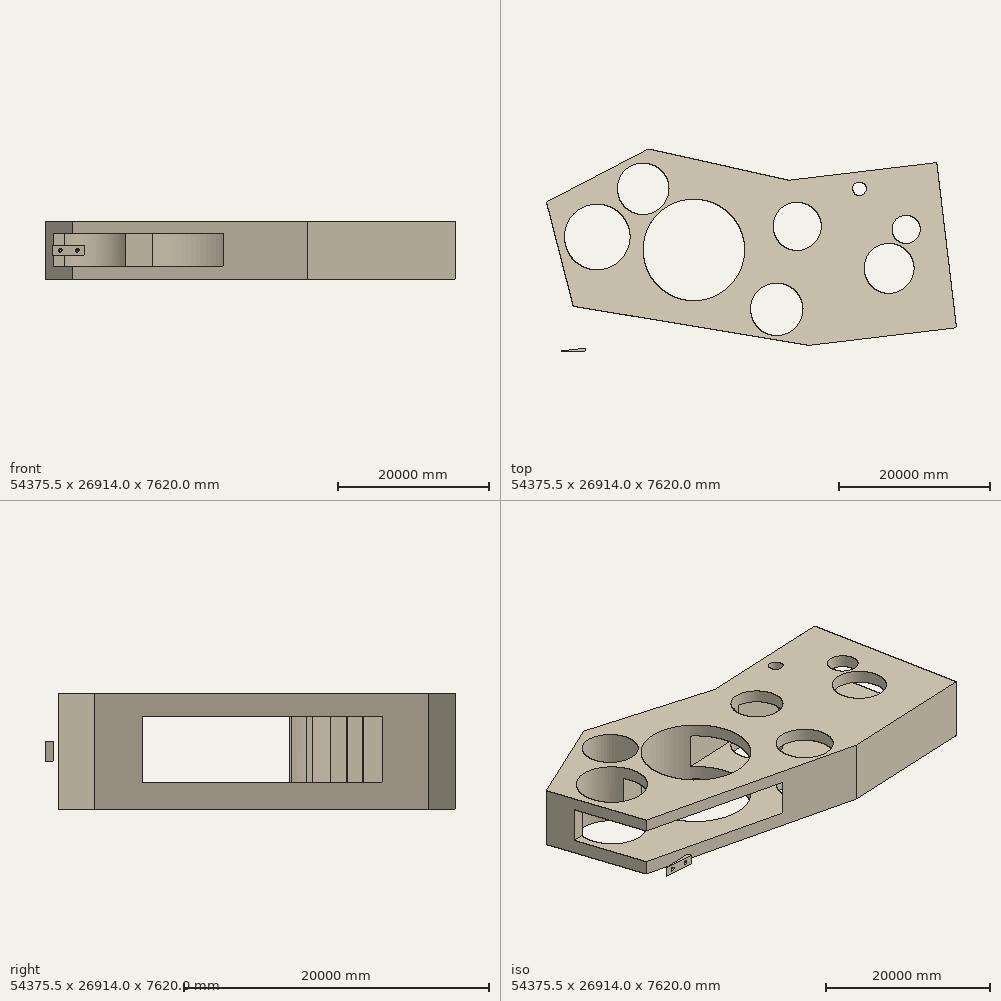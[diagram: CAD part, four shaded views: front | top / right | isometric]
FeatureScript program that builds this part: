
annotation { "Feature Type Name" : "Feature", "Feature Type Description" : "" }
export const myFeature = defineFeature(function(context is Context, id is Id, definition is map)
    precondition{}
    {
        {
            var Q0;
            Q0=qCreatedBy(makeId("Right.planeOp"),FACE);
            var sketch = newSketch(context, id + "F0", { "sketchPlane" : qUnion([Q0])});
            skCircle(sketch, "E0.cCircle", {"center": v(0, 0) * mm, "radius": 129.38 * mm, "construction": true});
            skLineSegment(sketch, "E0.0", {"start": v(-113.82, -61.52) * mm, "end": v(-128.36, -16.25) * mm});
            skLineSegment(sketch, "E0.1", {"start": v(-128.36, -16.25) * mm, "end": v(-125.56, 31.22) * mm});
            skLineSegment(sketch, "E0.2", {"start": v(-125.56, 31.22) * mm, "end": v(-105.8, 74.47) * mm});
            skLineSegment(sketch, "E0.3", {"start": v(-105.8, 74.47) * mm, "end": v(-71.76, 107.66) * mm});
            skLineSegment(sketch, "E0.4", {"start": v(-71.76, 107.66) * mm, "end": v(-28.02, 126.31) * mm});
            skLineSegment(sketch, "E0.5", {"start": v(-28.02, 126.31) * mm, "end": v(19.5, 127.9) * mm});
            skLineSegment(sketch, "E0.6", {"start": v(19.5, 127.9) * mm, "end": v(64.39, 112.22) * mm});
            skLineSegment(sketch, "E0.7", {"start": v(64.39, 112.22) * mm, "end": v(100.58, 81.38) * mm});
            skLineSegment(sketch, "E0.8", {"start": v(100.58, 81.38) * mm, "end": v(123.19, 39.55) * mm});
            skLineSegment(sketch, "E0.9", {"start": v(123.19, 39.55) * mm, "end": v(129.16, -7.62) * mm});
            skLineSegment(sketch, "E0.10", {"start": v(129.16, -7.62) * mm, "end": v(117.68, -53.76) * mm});
            skLineSegment(sketch, "E0.11", {"start": v(117.68, -53.76) * mm, "end": v(90.32, -92.64) * mm});
            skLineSegment(sketch, "E0.12", {"start": v(90.32, -92.64) * mm, "end": v(50.75, -119.01) * mm});
            skLineSegment(sketch, "E0.13", {"start": v(50.75, -119.01) * mm, "end": v(4.33, -129.3) * mm});
            skLineSegment(sketch, "E0.14", {"start": v(4.33, -129.3) * mm, "end": v(-42.67, -122.14) * mm});
            skLineSegment(sketch, "E0.15", {"start": v(-42.67, -122.14) * mm, "end": v(-83.91, -98.48) * mm});
            skLineSegment(sketch, "E0.16", {"start": v(-83.91, -98.48) * mm, "end": v(-113.82, -61.52) * mm});
            skLineSegment(sketch, "E1", {"start": v(-751.25, 452.87) * mm, "end": v(-751.25, -447.87) * mm, "construction": true});
            skSolve(sketch);
        }
        {
            var Q0;
            Q0 = qSketchRegion(id + "F0", true);
            var Q1;
            Q1=sQuery(id+"F0.wireOp",EDGE,"E1");
            revolve(context, id + "F1", {"entities" : qUnion([Q0]), "axis" : qUnion([Q1]), "revolveType" : RevolveType.FULL});
        }
        {
            var Q0;
            Q0=qCreatedBy(makeId("Top.planeOp"),FACE);
            var sketch = newSketch(context, id + "F2", { "sketchPlane" : qUnion([Q0])});
            skText(sketch, "E2", { "text": "Revolve", "fontName": "OpenSans-Regular.ttf"});
            const initialGuessF2  = {"E2": [1.73426, -1.17989, 1, 0, 0.20156]};
            skSetInitialGuess(sketch, initialGuessF2);
            skSolve(sketch);
        }
        {
            var Q0;
            Q0 = qSketchRegion(id + "F2", true);
            extrude(context, id + "F3", {"entities" : qUnion([Q0]), "endBound" : BoundingType.SYMMETRIC, "depth" : 25.4 * mm, "offsetDistance" : 25.4 * mm});
        }
        {
            var Q0;
            Q0=qCreatedBy(makeId("Top.planeOp"),FACE);
            var sketch = newSketch(context, id + "F4", { "sketchPlane" : qUnion([Q0])});
            skLineSegment(sketch, "E3.bottom", {"start": v(1860.44, -5644) * mm, "end": v(5331.7, -5644) * mm});
            skLineSegment(sketch, "E3.top", {"start": v(1860.44, -4642.66) * mm, "end": v(5331.7, -4642.66) * mm});
            skLineSegment(sketch, "E3.left", {"start": v(1860.44, -5644) * mm, "end": v(1860.44, -4642.66) * mm});
            skLineSegment(sketch, "E3.right", {"start": v(5331.7, -5644) * mm, "end": v(5331.7, -4642.66) * mm});
            skLineSegment(sketch, "E4.bottom", {"start": v(5331.7, -5644) * mm, "end": v(6333.03, -5644) * mm});
            skLineSegment(sketch, "E4.top", {"start": v(5331.7, -2172.74) * mm, "end": v(6333.03, -2172.74) * mm});
            skLineSegment(sketch, "E4.left", {"start": v(5331.7, -5644) * mm, "end": v(5331.7, -2172.74) * mm});
            skLineSegment(sketch, "E4.right", {"start": v(6333.03, -5644) * mm, "end": v(6333.03, -2172.74) * mm});
            skLineSegment(sketch, "E5", {"start": v(5331.7, -2601.31) * mm, "end": v(2527.28, -4642.66) * mm});
            skSolve(sketch);
        }
        {
            var Q0;
            {var subQ3=sQuery(id+"F4.wireOp",EDGE,"E4.bottom");Q0=makeQuery(id+"F4.imprint","IMPRINT",FACE,{"disambiguationData":[TD([[makeQuery(id+"F4.imprint","IMPRINT",EDGE,{"derivedFrom":subQ3}),1.0]])]});}
            var Q1;
            {var subQ5=sQuery(id+"F4.wireOp",EDGE,"E3.bottom");Q1=makeQuery(id+"F4.imprint","IMPRINT",FACE,{"disambiguationData":[TD([[makeQuery(id+"F4.imprint","IMPRINT",EDGE,{"derivedFrom":subQ5}),1.0]])]});}
            extrude(context, id + "F5", {"entities" : qUnion([Q0, Q1]), "endBound" : BoundingType.SYMMETRIC, "depth" : 1270 * mm, "offsetDistance" : 25.4 * mm});
        }
        {
            var Q0;
            {var subQ3=sQuery(id+"F4.wireOp",EDGE,"E5");Q0=makeQuery(id+"F4.imprint","IMPRINT",FACE,{"disambiguationData":[TD([[makeQuery(id+"F4.imprint","IMPRINT",EDGE,{"derivedFrom":subQ3}),1.0]])]});}
            extrude(context, id + "F6", {"entities" : qUnion([Q0]), "operationType" : NewBodyOperationType.ADD, "endBound" : BoundingType.SYMMETRIC, "depth" : 381 * mm, "offsetDistance" : 25.4 * mm});
        }
        {
            var Q0;
            Q0=makeQuery(id+"F5.opExtrude","SWEPT_FACE",FACE,{"disambiguationData":[OSD([sQuery(id+"F4.wireOp",EDGE,"E3.bottom"),sQuery(id+"F4.wireOp",EDGE,"E4.bottom")])]});
            var sketch = newSketch(context, id + "F7", { "sketchPlane" : qUnion([Q0])});
            skCircle(sketch, "E6", {"center": v(5326.56, 0) * mm, "radius": 337.34 * mm});
            skCircle(sketch, "E7", {"center": v(3121.87, 0) * mm, "radius": 337.34 * mm});
            skSolve(sketch);
        }
        {
            var Q0;
            Q0=sQuery(id+"F7.wireOp",VERTEX,"E7.center");
            var Q1;
            Q1=sQuery(id+"F7.wireOp",VERTEX,"E6.center");
            var Q2;
            Q2=makeQuery(id+"F5.opExtrude","SWEPT_BODY",BODY,{"disambiguationData":[OSD([sQuery(id+"F4.wireOp",EDGE,"E3.bottom"),sQuery(id+"F4.wireOp",EDGE,"E3.top"),sQuery(id+"F4.wireOp",EDGE,"E3.left"),sQuery(id+"F4.wireOp",EDGE,"E4.bottom"),sQuery(id+"F4.wireOp",EDGE,"E4.top"),sQuery(id+"F4.wireOp",EDGE,"E4.left"),sQuery(id+"F4.wireOp",EDGE,"E4.right")])]});
            hole(context, id + "F8", {"style" : HoleStyle.C_SINK, "endStyle" : HoleEndStyle.BLIND, "holeDiameter" : 254 * mm, "cSinkDiameter" : 508 * mm, "cSinkAngle" : 90 * degree, "majorDiameter" : 6.35 * mm, "holeDepth" : 381 * mm, "isTappedThrough" : true, "tappedDepth" : 12.7 * mm, "tapClearance" : 3, "startFromSketch" : true, "locations" : qUnion([Q0, Q1]), "scope" : qUnion([Q2])});
        }
        {
            var Q0;
            Q0=makeQuery(id+"F6.opExtrude","CAP_FACE",FACE,{"disambiguationData":[OSD([sQuery(id+"F4.wireOp",EDGE,"E3.top"),sQuery(id+"F4.wireOp",EDGE,"E4.left"),sQuery(id+"F4.wireOp",EDGE,"E5")])],"isStart":false});
            var Q1;
            Q1=makeQuery(id+"F6.opExtrude","CAP_FACE",FACE,{"disambiguationData":[OSD([sQuery(id+"F4.wireOp",EDGE,"E3.top"),sQuery(id+"F4.wireOp",EDGE,"E4.left"),sQuery(id+"F4.wireOp",EDGE,"E5")])],"isStart":true});
            chamfer(context, id + "F9", {"entities" : qUnion([Q0, Q1]), "width" : 101.6 * mm, "tangentPropagation" : true});
        }
        {
            var Q0;
            Q0=qCreatedBy(makeId("Top.planeOp"),FACE);
            var sketch = newSketch(context, id + "F10", { "sketchPlane" : qUnion([Q0])});
            skLineSegment(sketch, "E8", {"start": v(4663.22, 423.1) * mm, "end": v(35911.22, -4777.2) * mm});
            skLineSegment(sketch, "E9", {"start": v(35911.22, -4777.2) * mm, "end": v(33295.96, 17127.15) * mm});
            skLineSegment(sketch, "E10", {"start": v(33295.96, 17127.15) * mm, "end": v(14670.66, 21269.96) * mm});
            skLineSegment(sketch, "E11", {"start": v(14670.66, 21269.96) * mm, "end": v(1115.16, 14209) * mm});
            skLineSegment(sketch, "E12", {"start": v(1115.16, 14209) * mm, "end": v(4663.22, 423.1) * mm});
            skSolve(sketch);
        }
        {
            var Q0;
            Q0 = qSketchRegion(id + "F10", true);
            extrude(context, id + "F11", {"entities" : qUnion([Q0]), "endBound" : BoundingType.SYMMETRIC, "depth" : 7620 * mm, "offsetDistance" : 25.4 * mm});
        }
        {
            var Q0;
            Q0=makeQuery(id+"F11.opExtrude","CAP_FACE",FACE,{"disambiguationData":[OSD([sQuery(id+"F10.wireOp",EDGE,"E8"),sQuery(id+"F10.wireOp",EDGE,"E9"),sQuery(id+"F10.wireOp",EDGE,"E10"),sQuery(id+"F10.wireOp",EDGE,"E11"),sQuery(id+"F10.wireOp",EDGE,"E12")])],"isStart":false});
            var sketch = newSketch(context, id + "F12", { "sketchPlane" : qUnion([Q0])});
            skCircle(sketch, "E13", {"center": v(20670.27, 7875.97) * mm, "radius": 6734.16 * mm});
            skSolve(sketch);
        }
        {
            var Q0;
            Q0 = qSketchRegion(id + "F12", true);
            extrude(context, id + "F13", {"entities" : qUnion([Q0]), "operationType" : NewBodyOperationType.REMOVE, "oppositeDirection" : true, "depth" : 11680.36 * mm, "offsetDistance" : 25.4 * mm});
        }
        {
            var Q0;
            Q0=makeQuery(id+"F11.opExtrude","CAP_FACE",FACE,{"disambiguationData":[OSD([sQuery(id+"F10.wireOp",EDGE,"E8"),sQuery(id+"F10.wireOp",EDGE,"E9"),sQuery(id+"F10.wireOp",EDGE,"E10"),sQuery(id+"F10.wireOp",EDGE,"E11"),sQuery(id+"F10.wireOp",EDGE,"E12")])],"isStart":true});
            var sketch = newSketch(context, id + "F14", { "sketchPlane" : qUnion([Q0])});
            skCircle(sketch, "E14", {"center": v(7850.82, -9591.71) * mm, "radius": 4353.68 * mm});
            skSolve(sketch);
        }
        {
            var Q0;
            Q0 = qSketchRegion(id + "F14", true);
            extrude(context, id + "F15", {"entities" : qUnion([Q0]), "operationType" : NewBodyOperationType.REMOVE, "oppositeDirection" : true, "depth" : 10906.04 * mm, "offsetDistance" : 25.4 * mm});
        }
        {
            var Q0;
            Q0=makeQuery(id+"F11.opExtrude","CAP_FACE",FACE,{"disambiguationData":[OSD([sQuery(id+"F10.wireOp",EDGE,"E8"),sQuery(id+"F10.wireOp",EDGE,"E9"),sQuery(id+"F10.wireOp",EDGE,"E10"),sQuery(id+"F10.wireOp",EDGE,"E11"),sQuery(id+"F10.wireOp",EDGE,"E12")])],"isStart":false});
            var sketch = newSketch(context, id + "F16", { "sketchPlane" : qUnion([Q0])});
            skCircle(sketch, "E15", {"center": v(13945.7, 15984.27) * mm, "radius": 3419.9 * mm});
            skSolve(sketch);
        }
        {
            var Q0;
            Q0 = qSketchRegion(id + "F16", true);
            extrude(context, id + "F17", {"entities" : qUnion([Q0]), "operationType" : NewBodyOperationType.REMOVE, "endBound" : BoundingType.UP_TO_NEXT, "oppositeDirection" : true, "depth" : 25.4 * mm, "offsetDistance" : 25.4 * mm});
        }
        {
            var Q0;
            Q0=makeQuery(id+"F11.opExtrude","CAP_FACE",FACE,{"disambiguationData":[OSD([sQuery(id+"F10.wireOp",EDGE,"E8"),sQuery(id+"F10.wireOp",EDGE,"E9"),sQuery(id+"F10.wireOp",EDGE,"E10"),sQuery(id+"F10.wireOp",EDGE,"E11"),sQuery(id+"F10.wireOp",EDGE,"E12")])],"isStart":false});
            var sketch = newSketch(context, id + "F18", { "sketchPlane" : qUnion([Q0])});
            skCircle(sketch, "E16", {"center": v(31659.02, 0) * mm, "radius": 3478.28 * mm});
            skSolve(sketch);
        }
        {
            var Q0;
            Q0 = qSketchRegion(id + "F18", true);
            extrude(context, id + "F19", {"entities" : qUnion([Q0]), "operationType" : NewBodyOperationType.REMOVE, "endBound" : BoundingType.UP_TO_NEXT, "oppositeDirection" : true, "depth" : 25.4 * mm, "offsetDistance" : 25.4 * mm});
        }
        {
            var Q0;
            Q0=makeQuery(id+"F11.opExtrude","SWEPT_FACE",FACE,{"disambiguationData":[OSD([sQuery(id+"F10.wireOp",EDGE,"E9")])]});
            extrude(context, id + "F20", {"entities" : qUnion([Q0]), "operationType" : NewBodyOperationType.ADD, "depth" : 19718.52 * mm, "offsetDistance" : 25.4 * mm});
        }
        {
            var Q0;
            {var subQ0=sQuery(id+"F10.wireOp",EDGE,"E9");Q0=makeQuery(id+"F20.boolean.opBoolean","MERGE",FACE,{"derivedFrom":[makeQuery(id+"F11.opExtrude","CAP_FACE",FACE,{"disambiguationData":[OSD([sQuery(id+"F10.wireOp",EDGE,"E8"),subQ0,sQuery(id+"F10.wireOp",EDGE,"E10"),sQuery(id+"F10.wireOp",EDGE,"E11"),sQuery(id+"F10.wireOp",EDGE,"E12")])],"isStart":false}),makeQuery(id+"F20.opExtrude","SWEPT_FACE",FACE,{"disambiguationData":[OSD([subQ0]),TDD([makeQuery(id+"F11.opExtrude","CAP_EDGE",EDGE,{"disambiguationData":[OSD([subQ0])],"isStart":false})])]})]});}
            var sketch = newSketch(context, id + "F21", { "sketchPlane" : qUnion([Q0])});
            skCircle(sketch, "E17", {"center": v(34374.4, 11001.68) * mm, "radius": 3193.19 * mm});
            skCircle(sketch, "E18", {"center": v(42630.45, 15978.5) * mm, "radius": 905.48 * mm});
            skCircle(sketch, "E19", {"center": v(46555.97, 5432.74) * mm, "radius": 3311.88 * mm});
            skCircle(sketch, "E20", {"center": v(48830.28, 10592.78) * mm, "radius": 1873.98 * mm});
            skSolve(sketch);
        }
        {
            var Q0;
            Q0 = qSketchRegion(id + "F21", true);
            extrude(context, id + "F22", {"entities" : qUnion([Q0]), "operationType" : NewBodyOperationType.REMOVE, "endBound" : BoundingType.UP_TO_NEXT, "oppositeDirection" : true, "depth" : 25.4 * mm, "offsetDistance" : 25.4 * mm});
        }
        {
            var Q0;
            Q0=makeQuery(id+"F20.opExtrude","CAP_FACE",FACE,{"disambiguationData":[OSD([sQuery(id+"F10.wireOp",EDGE,"E9")])],"isStart":false});
            var sketch = newSketch(context, id + "F23", { "sketchPlane" : qUnion([Q0])});
            skLineSegment(sketch, "E21.bottom", {"start": v(-5841.52, 2272.64) * mm, "end": v(10018.88, 2272.64) * mm});
            skLineSegment(sketch, "E21.top", {"start": v(-5841.52, -2062.52) * mm, "end": v(10018.88, -2062.52) * mm});
            skLineSegment(sketch, "E21.left", {"start": v(-5841.52, 2272.64) * mm, "end": v(-5841.52, -2062.52) * mm});
            skLineSegment(sketch, "E21.right", {"start": v(10018.88, 2272.64) * mm, "end": v(10018.88, -2062.52) * mm});
            skSolve(sketch);
        }
        {
            var Q0;
            Q0 = qSketchRegion(id + "F23", true);
            extrude(context, id + "F24", {"entities" : qUnion([Q0]), "operationType" : NewBodyOperationType.REMOVE, "endBound" : BoundingType.THROUGH_ALL, "oppositeDirection" : true, "depth" : 25.4 * mm, "offsetDistance" : 25.4 * mm});
        }
    });
